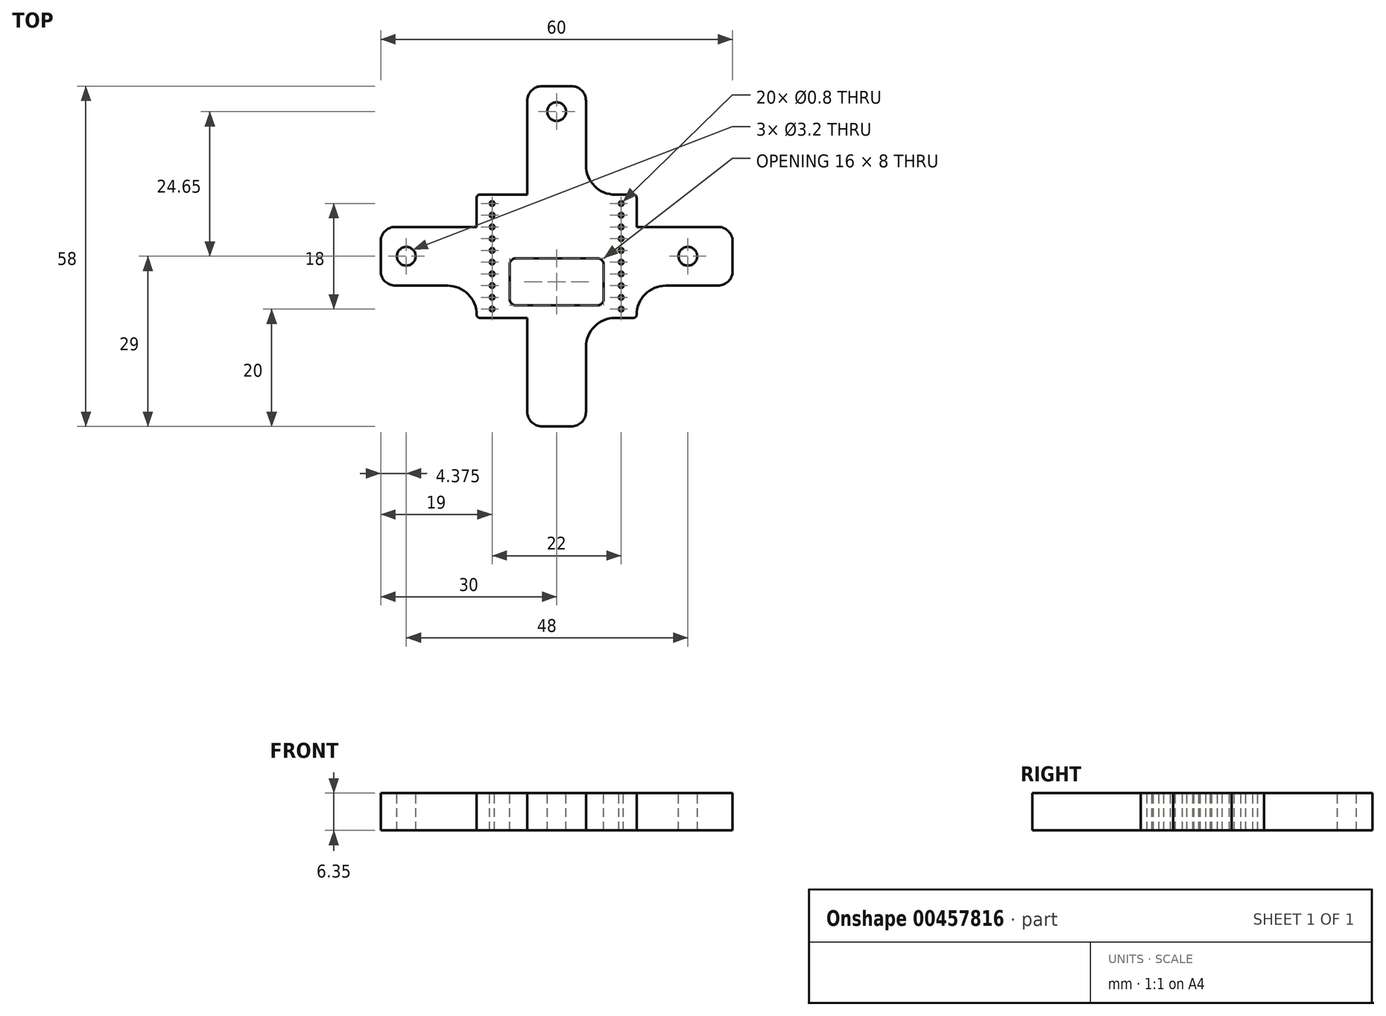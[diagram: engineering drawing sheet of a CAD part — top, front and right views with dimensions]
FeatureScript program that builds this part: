
annotation { "Feature Type Name" : "Feature", "Feature Type Description" : "" }
export const myFeature = defineFeature(function(context is Context, id is Id, definition is map)
    precondition{}
    {
        {
            var Q0;
            Q0=qCreatedBy(makeId("Top.planeOp"),FACE);
            var sketch = newSketch(context, id + "F0", { "sketchPlane" : qUnion([Q0])});
            skLineSegment(sketch, "E0.bottom", {"start": v(-13.62, 10.5) * mm, "end": v(13.62, 10.5) * mm});
            skLineSegment(sketch, "E0.top", {"start": v(-13.62, -10.5) * mm, "end": v(13.62, -10.5) * mm});
            skLineSegment(sketch, "E0.left", {"start": v(-13.62, 10.5) * mm, "end": v(-13.62, -10.5) * mm});
            skLineSegment(sketch, "E0.right", {"start": v(13.62, 10.5) * mm, "end": v(13.62, -10.5) * mm});
            skPoint(sketch, "E0.middle", {"position": v(0, 0) * mm});
            skSolve(sketch);
        }
        {
            var Q0;
            Q0 = qSketchRegion(id + "F0", true);
            extrude(context, id + "F1", {"entities" : qUnion([Q0]), "depth" : 6.35 * mm, "offsetDistance" : 25.4 * mm});
        }
        {
            var Q0;
            Q0=makeQuery(id+"F1.opExtrude","CAP_FACE",FACE,{"disambiguationData":[OSD([sQuery(id+"F0.wireOp",EDGE,"E0.bottom"),sQuery(id+"F0.wireOp",EDGE,"E0.top"),sQuery(id+"F0.wireOp",EDGE,"E0.left"),sQuery(id+"F0.wireOp",EDGE,"E0.right")])],"isStart":false});
            var sketch = newSketch(context, id + "F2", { "sketchPlane" : qUnion([Q0])});
            skCircle(sketch, "E1", {"center": v(11, 1) * mm, "radius": 0.4 * mm});
            skCircle(sketch, "E2.0.1.0", {"center": v(11, 3) * mm, "radius": 0.4 * mm});
            skCircle(sketch, "E2.0.2.0", {"center": v(11, 5) * mm, "radius": 0.4 * mm});
            skCircle(sketch, "E2.0.3.0", {"center": v(11, 7) * mm, "radius": 0.4 * mm});
            skCircle(sketch, "E2.0.4.0", {"center": v(11, 9) * mm, "radius": 0.4 * mm});
            skLineSegment(sketch, "E2.direction1", {"start": v(11, 1) * mm, "end": v(20.47, 1) * mm, "construction": true});
            skLineSegment(sketch, "E2.direction2", {"start": v(11, 1) * mm, "end": v(11, 3) * mm, "construction": true});
            skCircle(sketch, "E3.0.1.0", {"center": v(11, -1) * mm, "radius": 0.4 * mm});
            skCircle(sketch, "E3.0.2.0", {"center": v(11, -3) * mm, "radius": 0.4 * mm});
            skCircle(sketch, "E3.0.3.0", {"center": v(11, -5) * mm, "radius": 0.4 * mm});
            skCircle(sketch, "E3.0.4.0", {"center": v(11, -7) * mm, "radius": 0.4 * mm});
            skCircle(sketch, "E3.0.5.0", {"center": v(11, -9) * mm, "radius": 0.4 * mm});
            skLineSegment(sketch, "E3.direction1", {"start": v(11, 1) * mm, "end": v(36.4, 1) * mm, "construction": true});
            skLineSegment(sketch, "E3.direction2", {"start": v(11, 1) * mm, "end": v(11, -1) * mm, "construction": true});
            skLineSegment(sketch, "E4", {"start": v(0, 0) * mm, "end": v(0, 4.29) * mm, "construction": true});
            skCircle(sketch, "E5.MirrorC", {"center": v(-11, 9) * mm, "radius": 0.4 * mm});
            skCircle(sketch, "E6.MirrorC", {"center": v(-11, 7) * mm, "radius": 0.4 * mm});
            skCircle(sketch, "E7.MirrorC", {"center": v(-11, 5) * mm, "radius": 0.4 * mm});
            skCircle(sketch, "E8.MirrorC", {"center": v(-11, 3) * mm, "radius": 0.4 * mm});
            skCircle(sketch, "E9.MirrorC", {"center": v(-11, 1) * mm, "radius": 0.4 * mm});
            skCircle(sketch, "E10.MirrorC", {"center": v(-11, -1) * mm, "radius": 0.4 * mm});
            skCircle(sketch, "E11.MirrorC", {"center": v(-11, -3) * mm, "radius": 0.4 * mm});
            skCircle(sketch, "E12.MirrorC", {"center": v(-11, -5) * mm, "radius": 0.4 * mm});
            skCircle(sketch, "E13.MirrorC", {"center": v(-11, -7) * mm, "radius": 0.4 * mm});
            skCircle(sketch, "E14.MirrorC", {"center": v(-11, -9) * mm, "radius": 0.4 * mm});
            skSolve(sketch);
        }
        {
            var Q0;
            Q0 = qSketchRegion(id + "F2", true);
            extrude(context, id + "F3", {"entities" : qUnion([Q0]), "operationType" : NewBodyOperationType.REMOVE, "oppositeDirection" : true, "depth" : 25.4 * mm, "offsetDistance" : 25.4 * mm});
        }
        {
            var Q0;
            Q0=makeQuery(id+"F1.opExtrude","CAP_FACE",FACE,{"disambiguationData":[OSD([sQuery(id+"F0.wireOp",EDGE,"E0.bottom"),sQuery(id+"F0.wireOp",EDGE,"E0.top"),sQuery(id+"F0.wireOp",EDGE,"E0.left"),sQuery(id+"F0.wireOp",EDGE,"E0.right")])],"isStart":false});
            var sketch = newSketch(context, id + "F4", { "sketchPlane" : qUnion([Q0])});
            skLineSegment(sketch, "E15", {"start": v(0, 0) * mm, "end": v(0, 29) * mm, "construction": true});
            skLineSegment(sketch, "E16", {"start": v(0, 29) * mm, "end": v(-5, 29) * mm});
            skLineSegment(sketch, "E17", {"start": v(-5, 29) * mm, "end": v(-5, 10.5) * mm});
            skLineSegment(sketch, "E18", {"start": v(-5, 10.5) * mm, "end": v(0, 10.5) * mm});
            skLineSegment(sketch, "E19.MirrorCS", {"start": v(5, 29) * mm, "end": v(5, 10.5) * mm});
            skLineSegment(sketch, "E20.MirrorCS", {"start": v(5, 10.5) * mm, "end": v(0, 10.5) * mm});
            skLineSegment(sketch, "E21.MirrorCS", {"start": v(0, 29) * mm, "end": v(5, 29) * mm});
            skLineSegment(sketch, "E22", {"start": v(0, 0) * mm, "end": v(-6.34, 0) * mm, "construction": true});
            skLineSegment(sketch, "E23.MirrorCS", {"start": v(-5, -29) * mm, "end": v(-5, -10.5) * mm});
            skLineSegment(sketch, "E24.MirrorCS", {"start": v(-5, -10.5) * mm, "end": v(0, -10.5) * mm});
            skLineSegment(sketch, "E25.MirrorCS", {"start": v(5, -10.5) * mm, "end": v(0, -10.5) * mm});
            skLineSegment(sketch, "E26.MirrorCS", {"start": v(5, -29) * mm, "end": v(5, -10.5) * mm});
            skLineSegment(sketch, "E27.MirrorCS", {"start": v(0, -29) * mm, "end": v(5, -29) * mm});
            skLineSegment(sketch, "E28.MirrorCS", {"start": v(0, -29) * mm, "end": v(-5, -29) * mm});
            skLineSegment(sketch, "E29", {"start": v(0, 0) * mm, "end": v(-30, 0) * mm, "construction": true});
            skLineSegment(sketch, "E30", {"start": v(-30, 0) * mm, "end": v(-30, 5) * mm});
            skLineSegment(sketch, "E31", {"start": v(-30, 5) * mm, "end": v(-13.62, 5) * mm});
            skLineSegment(sketch, "E32", {"start": v(-13.62, 5) * mm, "end": v(-13.62, 0) * mm});
            skLineSegment(sketch, "E33.MirrorCS", {"start": v(-30, -5) * mm, "end": v(-13.62, -5) * mm});
            skLineSegment(sketch, "E34.MirrorCS", {"start": v(-30, 0) * mm, "end": v(-30, -5) * mm});
            skLineSegment(sketch, "E35.MirrorCS", {"start": v(-13.62, -5) * mm, "end": v(-13.62, 0) * mm});
            skLineSegment(sketch, "E36.MirrorCS", {"start": v(13.62, 5) * mm, "end": v(13.62, 0) * mm});
            skLineSegment(sketch, "E37.MirrorCS", {"start": v(30, 5) * mm, "end": v(13.62, 5) * mm});
            skLineSegment(sketch, "E38.MirrorCS", {"start": v(30, 0) * mm, "end": v(30, 5) * mm});
            skLineSegment(sketch, "E39.MirrorCS", {"start": v(30, 0) * mm, "end": v(30, -5) * mm});
            skLineSegment(sketch, "E40.MirrorCS", {"start": v(30, -5) * mm, "end": v(13.62, -5) * mm});
            skLineSegment(sketch, "E41.MirrorCS", {"start": v(13.62, -5) * mm, "end": v(13.62, 0) * mm});
            skSolve(sketch);
        }
        {
            var Q0;
            Q0 = qSketchRegion(id + "F4", true);
            extrude(context, id + "F5", {"entities" : qUnion([Q0]), "operationType" : NewBodyOperationType.ADD, "oppositeDirection" : true, "depth" : 6.35 * mm, "offsetDistance" : 25.4 * mm});
        }
        {
            var Q0;
            Q0=makeQuery(id+"F5.boolean.opBoolean","MERGE",FACE,{"derivedFrom":[makeQuery(id+"F1.opExtrude","CAP_FACE",FACE,{"disambiguationData":[OSD([sQuery(id+"F0.wireOp",EDGE,"E0.bottom"),sQuery(id+"F0.wireOp",EDGE,"E0.top"),sQuery(id+"F0.wireOp",EDGE,"E0.left"),sQuery(id+"F0.wireOp",EDGE,"E0.right")])],"isStart":false}),makeQuery(id+"F5.opExtrude","CAP_FACE",FACE,{"disambiguationData":[OSD([sQuery(id+"F4.wireOp",EDGE,"E16"),sQuery(id+"F4.wireOp",EDGE,"E17"),sQuery(id+"F4.wireOp",EDGE,"E18"),sQuery(id+"F4.wireOp",EDGE,"E19.MirrorCS"),sQuery(id+"F4.wireOp",EDGE,"E20.MirrorCS"),sQuery(id+"F4.wireOp",EDGE,"E21.MirrorCS")])],"isStart":true}),makeQuery(id+"F5.opExtrude","CAP_FACE",FACE,{"disambiguationData":[OSD([sQuery(id+"F4.wireOp",EDGE,"E23.MirrorCS"),sQuery(id+"F4.wireOp",EDGE,"E24.MirrorCS"),sQuery(id+"F4.wireOp",EDGE,"E25.MirrorCS"),sQuery(id+"F4.wireOp",EDGE,"E26.MirrorCS"),sQuery(id+"F4.wireOp",EDGE,"E27.MirrorCS"),sQuery(id+"F4.wireOp",EDGE,"E28.MirrorCS")])],"isStart":true}),makeQuery(id+"F5.opExtrude","CAP_FACE",FACE,{"disambiguationData":[OSD([sQuery(id+"F4.wireOp",EDGE,"E30"),sQuery(id+"F4.wireOp",EDGE,"E31"),sQuery(id+"F4.wireOp",EDGE,"E32"),sQuery(id+"F4.wireOp",EDGE,"E33.MirrorCS"),sQuery(id+"F4.wireOp",EDGE,"E34.MirrorCS"),sQuery(id+"F4.wireOp",EDGE,"E35.MirrorCS")])],"isStart":true}),makeQuery(id+"F5.opExtrude","CAP_FACE",FACE,{"disambiguationData":[OSD([sQuery(id+"F4.wireOp",EDGE,"E36.MirrorCS"),sQuery(id+"F4.wireOp",EDGE,"E37.MirrorCS"),sQuery(id+"F4.wireOp",EDGE,"E38.MirrorCS"),sQuery(id+"F4.wireOp",EDGE,"E39.MirrorCS"),sQuery(id+"F4.wireOp",EDGE,"E40.MirrorCS"),sQuery(id+"F4.wireOp",EDGE,"E41.MirrorCS")])],"isStart":true})]});
            var sketch = newSketch(context, id + "F6", { "sketchPlane" : qUnion([Q0])});
            skCircle(sketch, "E42", {"center": v(-25.63, 0) * mm, "radius": 1.6 * mm});
            skCircle(sketch, "E43", {"center": v(22.38, 0) * mm, "radius": 1.6 * mm});
            skCircle(sketch, "E44", {"center": v(0, 24.65) * mm, "radius": 1.6 * mm});
            skSolve(sketch);
        }
        {
            var Q0;
            Q0 = qSketchRegion(id + "F6", true);
            extrude(context, id + "F7", {"entities" : qUnion([Q0]), "operationType" : NewBodyOperationType.REMOVE, "oppositeDirection" : true, "depth" : 25.4 * mm});
        }
        {
            var Q0;
            Q0=makeQuery(id+"F5.opExtrude","SWEPT_EDGE",EDGE,{"disambiguationData":[OSD([sQuery(id+"F0.wireOp",EDGE,"E0.bottom"),sQuery(id+"F4.wireOp",EDGE,"E17"),sQuery(id+"F4.wireOp",EDGE,"E18")])]});
            var Q1;
            Q1=makeQuery(id+"F5.opExtrude","SWEPT_EDGE",EDGE,{"disambiguationData":[OSD([sQuery(id+"F0.wireOp",EDGE,"E0.left"),sQuery(id+"F4.wireOp",EDGE,"E31"),sQuery(id+"F4.wireOp",EDGE,"E32")])]});
            var Q2;
            Q2=makeQuery(id+"F5.opExtrude","SWEPT_EDGE",EDGE,{"disambiguationData":[OSD([sQuery(id+"F0.wireOp",EDGE,"E0.left"),sQuery(id+"F4.wireOp",EDGE,"E33.MirrorCS"),sQuery(id+"F4.wireOp",EDGE,"E35.MirrorCS")])]});
            var Q3;
            Q3=makeQuery(id+"F5.opExtrude","SWEPT_EDGE",EDGE,{"disambiguationData":[OSD([sQuery(id+"F0.wireOp",EDGE,"E0.top"),sQuery(id+"F4.wireOp",EDGE,"E23.MirrorCS"),sQuery(id+"F4.wireOp",EDGE,"E24.MirrorCS")])]});
            var Q4;
            Q4=makeQuery(id+"F5.opExtrude","SWEPT_EDGE",EDGE,{"disambiguationData":[OSD([sQuery(id+"F0.wireOp",EDGE,"E0.bottom"),sQuery(id+"F4.wireOp",EDGE,"E19.MirrorCS"),sQuery(id+"F4.wireOp",EDGE,"E20.MirrorCS")])]});
            var Q5;
            Q5=makeQuery(id+"F5.opExtrude","SWEPT_EDGE",EDGE,{"disambiguationData":[OSD([sQuery(id+"F0.wireOp",EDGE,"E0.right"),sQuery(id+"F4.wireOp",EDGE,"E36.MirrorCS"),sQuery(id+"F4.wireOp",EDGE,"E37.MirrorCS")])]});
            var Q6;
            Q6=makeQuery(id+"F5.opExtrude","SWEPT_EDGE",EDGE,{"disambiguationData":[OSD([sQuery(id+"F0.wireOp",EDGE,"E0.right"),sQuery(id+"F4.wireOp",EDGE,"E40.MirrorCS"),sQuery(id+"F4.wireOp",EDGE,"E41.MirrorCS")])]});
            var Q7;
            Q7=makeQuery(id+"F5.opExtrude","SWEPT_EDGE",EDGE,{"disambiguationData":[OSD([sQuery(id+"F0.wireOp",EDGE,"E0.top"),sQuery(id+"F4.wireOp",EDGE,"E25.MirrorCS"),sQuery(id+"F4.wireOp",EDGE,"E26.MirrorCS")])]});
            fillet(context, id + "F8", {"entities" : qUnion([Q0, Q1, Q2, Q3, Q4, Q5, Q6, Q7]), "radius" : 5 * mm, "tangentPropagation" : true, "allowEdgeOverflow" : false});
        }
        {
            var Q0;
            Q0=makeQuery(id+"F5.opExtrude","SWEPT_EDGE",EDGE,{"disambiguationData":[OSD([sQuery(id+"F4.wireOp",EDGE,"E30"),sQuery(id+"F4.wireOp",EDGE,"E31")])]});
            var Q1;
            Q1=makeQuery(id+"F5.opExtrude","SWEPT_EDGE",EDGE,{"disambiguationData":[OSD([sQuery(id+"F4.wireOp",EDGE,"E16"),sQuery(id+"F4.wireOp",EDGE,"E17")])]});
            var Q2;
            Q2=makeQuery(id+"F5.opExtrude","SWEPT_EDGE",EDGE,{"disambiguationData":[OSD([sQuery(id+"F4.wireOp",EDGE,"E19.MirrorCS"),sQuery(id+"F4.wireOp",EDGE,"E21.MirrorCS")])]});
            var Q3;
            Q3=makeQuery(id+"F5.opExtrude","SWEPT_EDGE",EDGE,{"disambiguationData":[OSD([sQuery(id+"F4.wireOp",EDGE,"E33.MirrorCS"),sQuery(id+"F4.wireOp",EDGE,"E34.MirrorCS")])]});
            var Q4;
            Q4=makeQuery(id+"F5.opExtrude","SWEPT_EDGE",EDGE,{"disambiguationData":[OSD([sQuery(id+"F4.wireOp",EDGE,"E23.MirrorCS"),sQuery(id+"F4.wireOp",EDGE,"E28.MirrorCS")])]});
            var Q5;
            Q5=makeQuery(id+"F5.opExtrude","SWEPT_EDGE",EDGE,{"disambiguationData":[OSD([sQuery(id+"F4.wireOp",EDGE,"E26.MirrorCS"),sQuery(id+"F4.wireOp",EDGE,"E27.MirrorCS")])]});
            var Q6;
            Q6=makeQuery(id+"F5.opExtrude","SWEPT_EDGE",EDGE,{"disambiguationData":[OSD([sQuery(id+"F4.wireOp",EDGE,"E37.MirrorCS"),sQuery(id+"F4.wireOp",EDGE,"E38.MirrorCS")])]});
            var Q7;
            Q7=makeQuery(id+"F5.opExtrude","SWEPT_EDGE",EDGE,{"disambiguationData":[OSD([sQuery(id+"F4.wireOp",EDGE,"E39.MirrorCS"),sQuery(id+"F4.wireOp",EDGE,"E40.MirrorCS")])]});
            fillet(context, id + "F9", {"entities" : qUnion([Q0, Q1, Q2, Q3, Q4, Q5, Q6, Q7]), "radius" : 2.5 * mm, "tangentPropagation" : true, "allowEdgeOverflow" : false});
        }
        {
            var Q0;
            Q0=makeQuery(id+"F1.opExtrude","SWEPT_EDGE",EDGE,{"disambiguationData":[OSD([sQuery(id+"F0.wireOp",EDGE,"E0.top"),sQuery(id+"F0.wireOp",EDGE,"E0.left")])]});
            var Q1;
            Q1=makeQuery(id+"F1.opExtrude","SWEPT_EDGE",EDGE,{"disambiguationData":[OSD([sQuery(id+"F0.wireOp",EDGE,"E0.top"),sQuery(id+"F0.wireOp",EDGE,"E0.right")])]});
            var Q2;
            Q2=makeQuery(id+"F1.opExtrude","SWEPT_EDGE",EDGE,{"disambiguationData":[OSD([sQuery(id+"F0.wireOp",EDGE,"E0.bottom"),sQuery(id+"F0.wireOp",EDGE,"E0.left")])]});
            var Q3;
            Q3=makeQuery(id+"F1.opExtrude","SWEPT_EDGE",EDGE,{"disambiguationData":[OSD([sQuery(id+"F0.wireOp",EDGE,"E0.bottom"),sQuery(id+"F0.wireOp",EDGE,"E0.right")])]});
            fillet(context, id + "F10", {"entities" : qUnion([Q0, Q1, Q2, Q3]), "radius" : .5 * mm, "tangentPropagation" : true, "allowEdgeOverflow" : false});
        }
        {
            var Q0;
            Q0=makeQuery(id+"F5.boolean.opBoolean","MERGE",FACE,{"derivedFrom":[makeQuery(id+"F1.opExtrude","CAP_FACE",FACE,{"disambiguationData":[OSD([sQuery(id+"F0.wireOp",EDGE,"E0.bottom"),sQuery(id+"F0.wireOp",EDGE,"E0.top"),sQuery(id+"F0.wireOp",EDGE,"E0.left"),sQuery(id+"F0.wireOp",EDGE,"E0.right")])],"isStart":false}),makeQuery(id+"F5.opExtrude","CAP_FACE",FACE,{"disambiguationData":[OSD([sQuery(id+"F4.wireOp",EDGE,"E16"),sQuery(id+"F4.wireOp",EDGE,"E17"),sQuery(id+"F4.wireOp",EDGE,"E18"),sQuery(id+"F4.wireOp",EDGE,"E19.MirrorCS"),sQuery(id+"F4.wireOp",EDGE,"E20.MirrorCS"),sQuery(id+"F4.wireOp",EDGE,"E21.MirrorCS")])],"isStart":true}),makeQuery(id+"F5.opExtrude","CAP_FACE",FACE,{"disambiguationData":[OSD([sQuery(id+"F4.wireOp",EDGE,"E23.MirrorCS"),sQuery(id+"F4.wireOp",EDGE,"E24.MirrorCS"),sQuery(id+"F4.wireOp",EDGE,"E25.MirrorCS"),sQuery(id+"F4.wireOp",EDGE,"E26.MirrorCS"),sQuery(id+"F4.wireOp",EDGE,"E27.MirrorCS"),sQuery(id+"F4.wireOp",EDGE,"E28.MirrorCS")])],"isStart":true}),makeQuery(id+"F5.opExtrude","CAP_FACE",FACE,{"disambiguationData":[OSD([sQuery(id+"F4.wireOp",EDGE,"E30"),sQuery(id+"F4.wireOp",EDGE,"E31"),sQuery(id+"F4.wireOp",EDGE,"E32"),sQuery(id+"F4.wireOp",EDGE,"E33.MirrorCS"),sQuery(id+"F4.wireOp",EDGE,"E34.MirrorCS"),sQuery(id+"F4.wireOp",EDGE,"E35.MirrorCS")])],"isStart":true}),makeQuery(id+"F5.opExtrude","CAP_FACE",FACE,{"disambiguationData":[OSD([sQuery(id+"F4.wireOp",EDGE,"E36.MirrorCS"),sQuery(id+"F4.wireOp",EDGE,"E37.MirrorCS"),sQuery(id+"F4.wireOp",EDGE,"E38.MirrorCS"),sQuery(id+"F4.wireOp",EDGE,"E39.MirrorCS"),sQuery(id+"F4.wireOp",EDGE,"E40.MirrorCS"),sQuery(id+"F4.wireOp",EDGE,"E41.MirrorCS")])],"isStart":true})]});
            var sketch = newSketch(context, id + "F11", { "sketchPlane" : qUnion([Q0])});
            skLineSegment(sketch, "E45.bottom", {"start": v(-7, -0.35) * mm, "end": v(7, -0.35) * mm});
            skLineSegment(sketch, "E45.top", {"start": v(-7, -8.35) * mm, "end": v(7, -8.35) * mm});
            skLineSegment(sketch, "E45.left", {"start": v(-8, -1.35) * mm, "end": v(-8, -7.35) * mm});
            skLineSegment(sketch, "E45.right", {"start": v(8, -1.35) * mm, "end": v(8, -7.35) * mm});
            skPoint(sketch, "E46.visualSharp", {"position": v(-8, -0.35) * mm});
            skArc(sketch, "E46.filletArc", {"start": v(-7, -0.35) * mm, "mid": v(-7.7, -0.64) * mm, "end": v(-8, -1.35) * mm});
            skPoint(sketch, "E47.visualSharp", {"position": v(8, -0.35) * mm});
            skArc(sketch, "E47.filletArc", {"start": v(8, -1.35) * mm, "mid": v(7.7, -0.64) * mm, "end": v(7, -0.35) * mm});
            skPoint(sketch, "E48.visualSharp", {"position": v(8, -8.35) * mm});
            skArc(sketch, "E48.filletArc", {"start": v(7, -8.35) * mm, "mid": v(7.7, -8.06) * mm, "end": v(8, -7.35) * mm});
            skPoint(sketch, "E49.visualSharp", {"position": v(-8, -8.35) * mm});
            skArc(sketch, "E49.filletArc", {"start": v(-8, -7.35) * mm, "mid": v(-7.7, -8.06) * mm, "end": v(-7, -8.35) * mm});
            skSolve(sketch);
        }
        {
            var Q0;
            Q0 = qSketchRegion(id + "F11", true);
            extrude(context, id + "F12", {"entities" : qUnion([Q0]), "operationType" : NewBodyOperationType.REMOVE, "oppositeDirection" : true, "depth" : 25.4 * mm, "offsetDistance" : 25.4 * mm});
        }
    });
